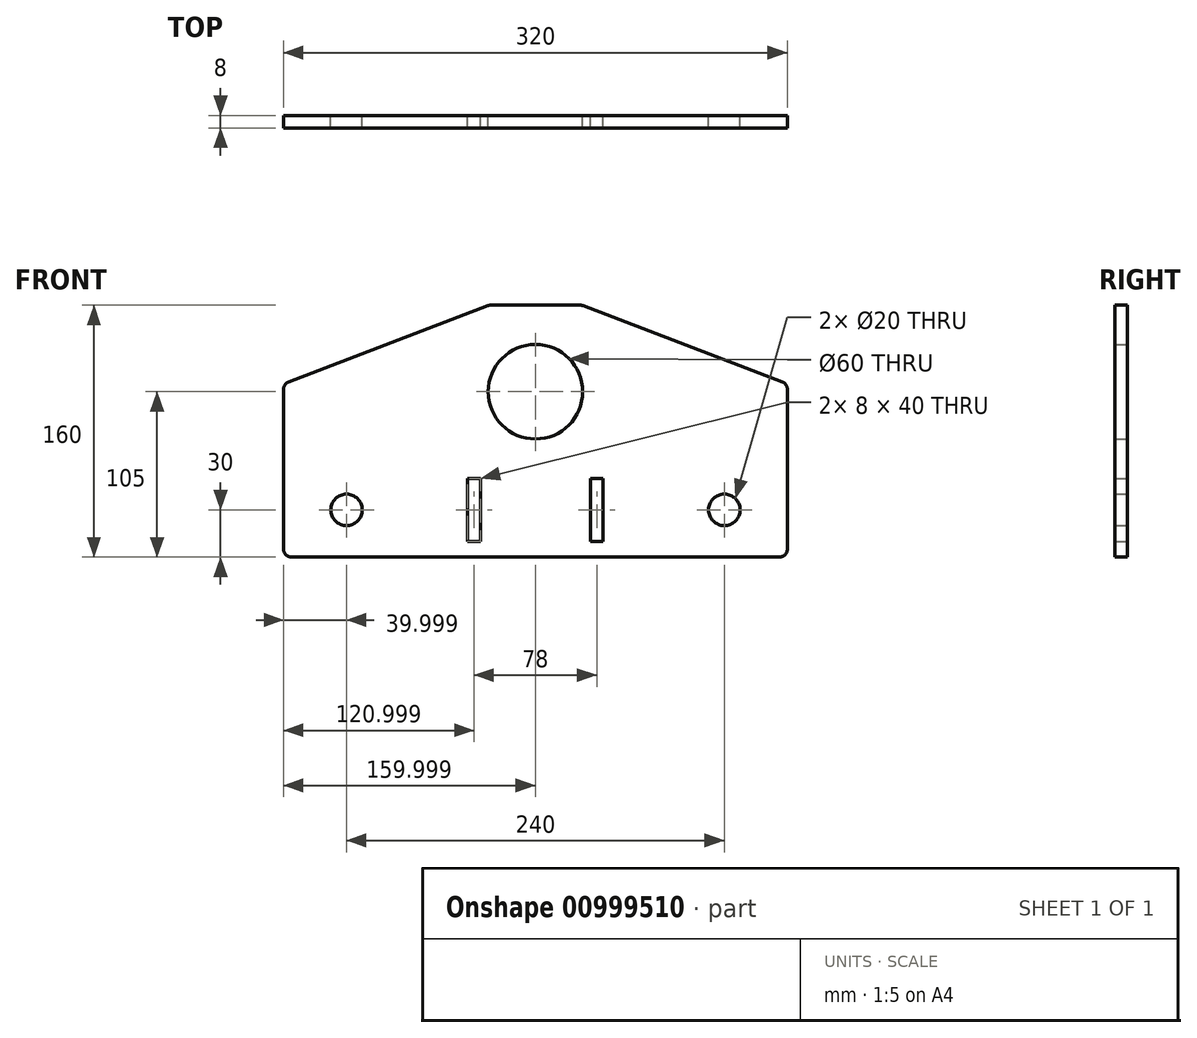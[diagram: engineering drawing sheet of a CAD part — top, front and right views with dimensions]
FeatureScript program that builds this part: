
annotation { "Feature Type Name" : "Feature", "Feature Type Description" : "" }
export const myFeature = defineFeature(function(context is Context, id is Id, definition is map)
    precondition{}
    {
        {
            var Q0;
            Q0=qCreatedBy(makeId("Front.planeOp"),FACE);
            var sketch = newSketch(context, id + "F0", { "sketchPlane" : qUnion([Q0])});
            skLineSegment(sketch, "E0", {"start": v(-115.9, -160) * mm, "end": v(204.1, -160) * mm});
            skLineSegment(sketch, "E1", {"start": v(204.1, -160) * mm, "end": v(204.1, -50) * mm});
            skLineSegment(sketch, "E2", {"start": v(204.1, -50) * mm, "end": v(73.34, 0) * mm});
            skLineSegment(sketch, "E3", {"start": v(73.34, 0) * mm, "end": v(14.88, 0) * mm});
            skLineSegment(sketch, "E4", {"start": v(14.88, 0) * mm, "end": v(-115.9, -50) * mm});
            skLineSegment(sketch, "E5", {"start": v(-115.9, -50) * mm, "end": v(-115.9, -160) * mm});
            skCircle(sketch, "E6", {"center": v(44.1, -55) * mm, "radius": 30 * mm});
            skPoint(sketch, "E6.centerSnap0", {"position": v(44.1, -160) * mm});
            skCircle(sketch, "E7", {"center": v(164.1, -130) * mm, "radius": 10 * mm});
            skCircle(sketch, "E8", {"center": v(-75.9, -130) * mm, "radius": 10 * mm});
            skLineSegment(sketch, "E9.bottom", {"start": v(87.1, -110) * mm, "end": v(79.1, -110) * mm});
            skLineSegment(sketch, "E9.top", {"start": v(87.1, -150) * mm, "end": v(79.1, -150) * mm});
            skLineSegment(sketch, "E9.left", {"start": v(87.1, -110) * mm, "end": v(87.1, -150) * mm});
            skLineSegment(sketch, "E9.right", {"start": v(79.1, -110) * mm, "end": v(79.1, -150) * mm});
            skLineSegment(sketch, "E10.bottom", {"start": v(9.1, -110) * mm, "end": v(1.1, -110) * mm});
            skLineSegment(sketch, "E10.top", {"start": v(9.1, -150) * mm, "end": v(1.1, -150) * mm});
            skLineSegment(sketch, "E10.left", {"start": v(9.1, -110) * mm, "end": v(9.1, -150) * mm});
            skLineSegment(sketch, "E10.right", {"start": v(1.1, -110) * mm, "end": v(1.1, -150) * mm});
            skSolve(sketch);
        }
        {
            var Q0;
            Q0=makeQuery(id+"F0.imprint","IMPRINT",FACE,{"disambiguationData":[TD([[makeQuery(id+"F0.imprint","IMPRINT",EDGE,{"derivedFrom":sQuery(id+"F0.wireOp",EDGE,"E0")}),1.0]])]});
            extrude(context, id + "F1", {"entities" : qUnion([Q0]), "depth" : 8 * mm, "offsetDistance" : 25 * mm});
        }
        {
            var Q0;
            Q0=makeQuery(id+"F1.opExtrude","SWEPT_EDGE",EDGE,{"disambiguationData":[OSD([sQuery(id+"F0.wireOp",EDGE,"E4"),sQuery(id+"F0.wireOp",EDGE,"E5")])]});
            var Q1;
            Q1=makeQuery(id+"F1.opExtrude","SWEPT_EDGE",EDGE,{"disambiguationData":[OSD([sQuery(id+"F0.wireOp",EDGE,"E3"),sQuery(id+"F0.wireOp",EDGE,"E4")])]});
            var Q2;
            Q2=makeQuery(id+"F1.opExtrude","SWEPT_EDGE",EDGE,{"disambiguationData":[OSD([sQuery(id+"F0.wireOp",EDGE,"E1"),sQuery(id+"F0.wireOp",EDGE,"E2")])]});
            var Q3;
            Q3=makeQuery(id+"F1.opExtrude","SWEPT_EDGE",EDGE,{"disambiguationData":[OSD([sQuery(id+"F0.wireOp",EDGE,"E0"),sQuery(id+"F0.wireOp",EDGE,"E1")])]});
            var Q4;
            Q4=makeQuery(id+"F1.opExtrude","SWEPT_EDGE",EDGE,{"disambiguationData":[OSD([sQuery(id+"F0.wireOp",EDGE,"E0"),sQuery(id+"F0.wireOp",EDGE,"E5")])]});
            var Q5;
            Q5=makeQuery(id+"F1.opExtrude","SWEPT_EDGE",EDGE,{"disambiguationData":[OSD([sQuery(id+"F0.wireOp",EDGE,"E2"),sQuery(id+"F0.wireOp",EDGE,"E3")])]});
            fillet(context, id + "F2", {"entities" : qUnion([Q0, Q1, Q2, Q3, Q4, Q5]), "radius" : 5 * mm, "tangentPropagation" : true, "defaultsChanged" : false, "vertexSettings" : [], "allowEdgeOverflow" : false});
        }
    });
